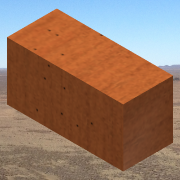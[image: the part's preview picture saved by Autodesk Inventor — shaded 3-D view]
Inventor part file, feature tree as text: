
AUTODESK INVENTOR PART (.ipt)
format: ipt  version: 2014 SP1 (Build 180222100, 222)  size: 124,416 bytes
history: native  units: in
note: dims shown in document units (in); Inventor stores cm internally (conversion verified against a paired STEP export)
features: extrude x1, sketch x1
ambient origin geometry x8: Origin, YZ Plane, XZ Plane, XY Plane, X Axis, Y Axis, Z Axis, Center Point
bodies: Solid1 (feature_tree)
feature tree (2):
  extrude  "Extrusion1"  Depth=1.75in
  sketch  "Sketch1"  dims[d0=3.5in d1=1.75in d2=1.5in d3=0.0in]
